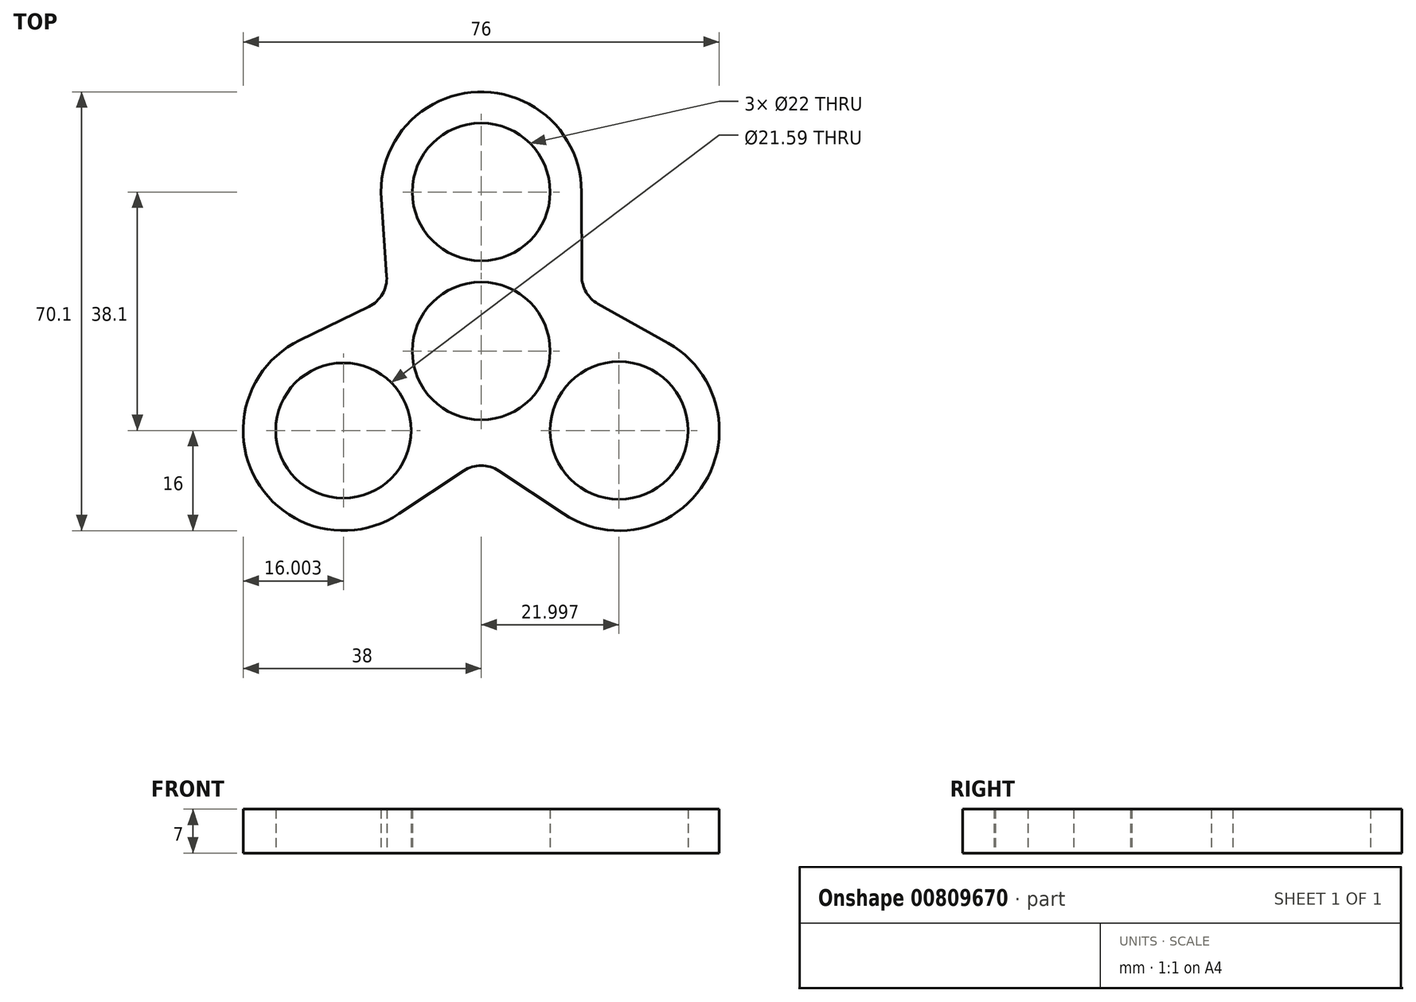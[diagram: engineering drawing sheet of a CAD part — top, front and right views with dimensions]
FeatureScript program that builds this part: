
annotation { "Feature Type Name" : "Feature", "Feature Type Description" : "" }
export const myFeature = defineFeature(function(context is Context, id is Id, definition is map)
    precondition{}
    {
        {
            var Q0;
            Q0=qCreatedBy(makeId("Top.planeOp"),FACE);
            var sketch = newSketch(context, id + "F0", { "sketchPlane" : qUnion([Q0])});
            skCircle(sketch, "E0", {"center": v(0, 25.4) * mm, "radius": 11 * mm});
            skCircle(sketch, "E1", {"center": v(0, 0) * mm, "radius": 11 * mm});
            skCircle(sketch, "E2", {"center": v(-22, -12.7) * mm, "radius": 10.8 * mm});
            skCircle(sketch, "E3", {"center": v(22, -12.7) * mm, "radius": 11 * mm});
            skArc(sketch, "E4.0", {"start": v(-29, 1.68) * mm, "mid": v(-35.88, -20.65) * mm, "end": v(-13.13, -26.02) * mm});
            skArc(sketch, "E5.0", {"start": v(16, 25.45) * mm, "mid": v(-0.59, 41.39) * mm, "end": v(-15.96, 24.28) * mm});
            skArc(sketch, "E6.0", {"start": v(13.13, -26.02) * mm, "mid": v(35.64, -21.06) * mm, "end": v(29.83, 1.25) * mm});
            skLineSegment(sketch, "E7", {"start": v(-13.13, -26.02) * mm, "end": v(0, -17.28) * mm});
            skLineSegment(sketch, "E8", {"start": v(13.13, -26.02) * mm, "end": v(0, -17.28) * mm});
            skLineSegment(sketch, "E9", {"start": v(-29, 1.68) * mm, "end": v(-14.86, 8.58) * mm});
            skLineSegment(sketch, "E10", {"start": v(-15.96, 24.28) * mm, "end": v(-14.86, 8.58) * mm});
            skLineSegment(sketch, "E11", {"start": v(16, 25.45) * mm, "end": v(16.05, 9) * mm});
            skLineSegment(sketch, "E12", {"start": v(29.83, 1.25) * mm, "end": v(16.05, 9) * mm});
            skLineSegment(sketch, "E13", {"start": v(22, -12.7) * mm, "end": v(0, 0) * mm});
            skLineSegment(sketch, "E14", {"start": v(0, 0) * mm, "end": v(0, 25.4) * mm});
            skLineSegment(sketch, "E15", {"start": v(0, 0) * mm, "end": v(-22, -12.7) * mm});
            skSolve(sketch);
        }
        {
            var Q0;
            Q0=makeQuery(id+"F0.imprint","IMPRINT",FACE,{"disambiguationData":[TD([[makeQuery(id+"F0.imprint","IMPRINT",EDGE,{"derivedFrom":sQuery(id+"F0.wireOp",EDGE,"E0")}),-1.0]])]});
            extrude(context, id + "F1", {"entities" : qUnion([Q0]), "depth" : 7 * mm, "offsetDistance" : 25.4 * mm});
        }
        {
            var Q0;
            Q0=makeQuery(id+"F1.opExtrude","SWEPT_EDGE",EDGE,{"disambiguationData":[OSD([sQuery(id+"F0.wireOp",EDGE,"E9"),sQuery(id+"F0.wireOp",EDGE,"E10")])]});
            var Q1;
            Q1=makeQuery(id+"F1.opExtrude","SWEPT_EDGE",EDGE,{"disambiguationData":[OSD([sQuery(id+"F0.wireOp",EDGE,"E11"),sQuery(id+"F0.wireOp",EDGE,"E12")])]});
            var Q2;
            Q2=makeQuery(id+"F1.opExtrude","SWEPT_EDGE",EDGE,{"disambiguationData":[OSD([sQuery(id+"F0.wireOp",EDGE,"E7"),sQuery(id+"F0.wireOp",EDGE,"E8")])]});
            fillet(context, id + "F2", {"entities" : qUnion([Q0, Q1, Q2]), "radius" : 5.08 * mm, "tangentPropagation" : true, "allowEdgeOverflow" : false});
        }
    });
